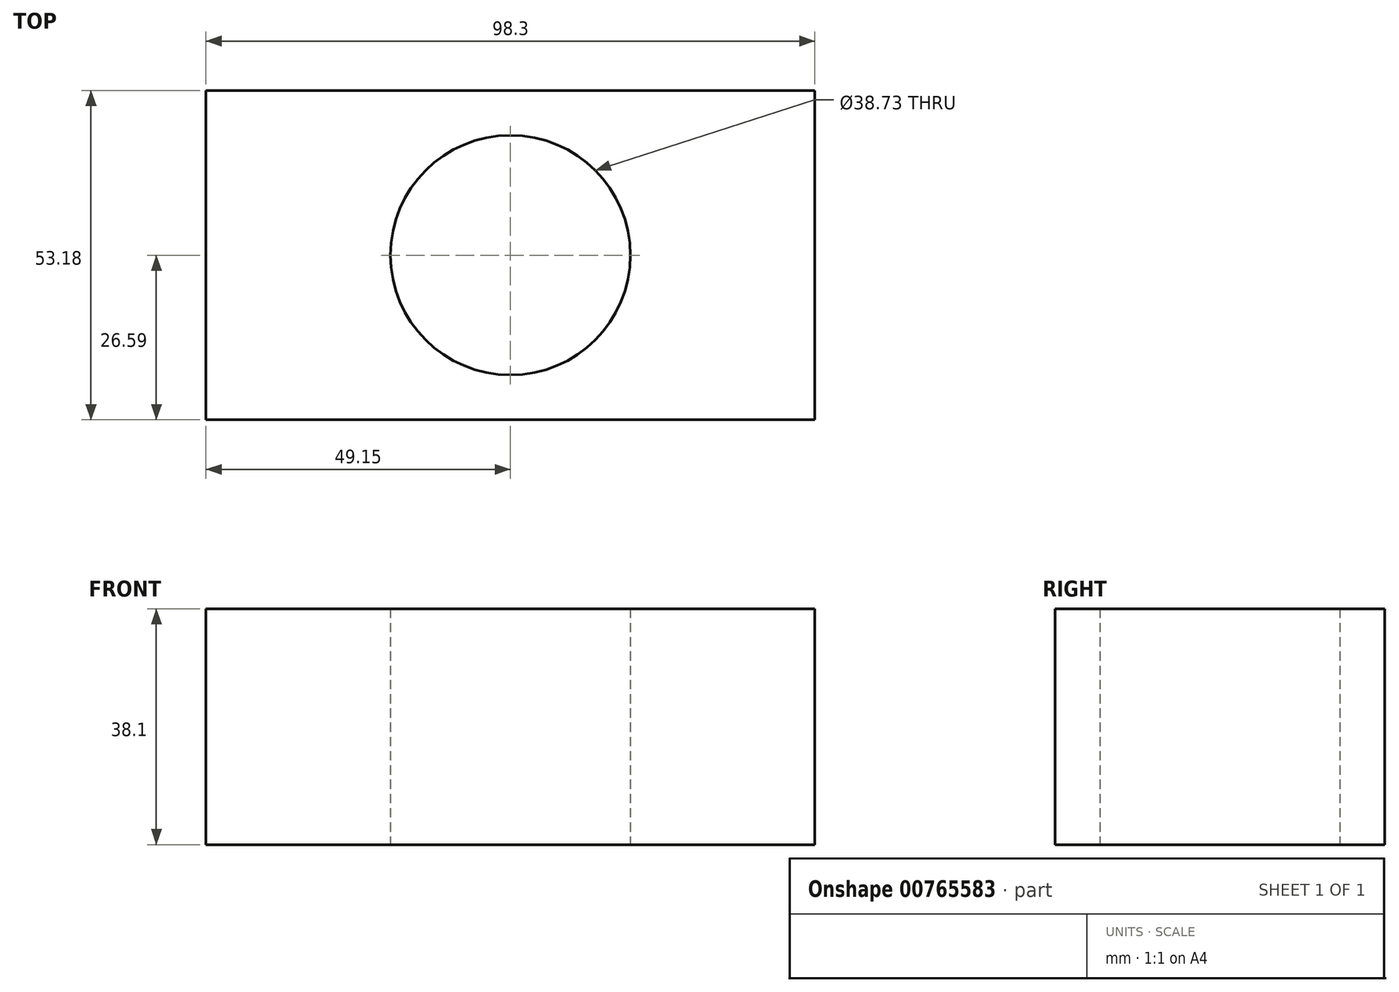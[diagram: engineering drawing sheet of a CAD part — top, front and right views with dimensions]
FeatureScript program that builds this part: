
annotation { "Feature Type Name" : "Feature", "Feature Type Description" : "" }
export const myFeature = defineFeature(function(context is Context, id is Id, definition is map)
    precondition{}
    {
        {
            var Q0;
            Q0=qCreatedBy(makeId("Top.planeOp"),FACE);
            var sketch = newSketch(context, id + "F0", { "sketchPlane" : qUnion([Q0])});
            skLineSegment(sketch, "E0.bottom", {"start": v(49.15, -26.59) * mm, "end": v(-49.15, -26.59) * mm});
            skLineSegment(sketch, "E0.top", {"start": v(49.15, 26.59) * mm, "end": v(-49.15, 26.59) * mm});
            skLineSegment(sketch, "E0.left", {"start": v(49.15, -26.59) * mm, "end": v(49.15, 26.59) * mm});
            skLineSegment(sketch, "E0.right", {"start": v(-49.15, -26.59) * mm, "end": v(-49.15, 26.59) * mm});
            skPoint(sketch, "E0.middle", {"position": v(0, 0) * mm});
            skCircle(sketch, "E1", {"center": v(0, 0) * mm, "radius": 19.36 * mm});
            skSolve(sketch);
        }
        {
            var Q0;
            Q0=makeQuery(id+"F0.imprint","IMPRINT",FACE,{"disambiguationData":[TD([[makeQuery(id+"F0.imprint","IMPRINT",EDGE,{"derivedFrom":sQuery(id+"F0.wireOp",EDGE,"E0.bottom")}),-1.0]])]});
            extrude(context, id + "F1", {"entities" : qUnion([Q0]), "depth" : 38.1 * mm, "offsetDistance" : 25.4 * mm});
        }
    });
